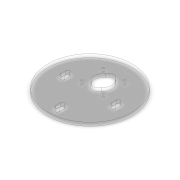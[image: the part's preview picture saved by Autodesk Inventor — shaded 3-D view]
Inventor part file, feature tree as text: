
AUTODESK INVENTOR PART (.ipt)
format: ipt  version: 2020 (Build 240168000, 168)  size: 187,904 bytes
history: native  units: in
note: dims shown in document units (in); Inventor stores cm internally (conversion verified against a paired STEP export)
features: extrude x1
ambient origin geometry x8: Origin, YZ Plane, XZ Plane, XY Plane, X Axis, Y Axis, Z Axis, Center Point
bodies: Body1 (feature_tree)
feature tree (1):
  extrude  "Extrusion4"  Depth=1.2205in
